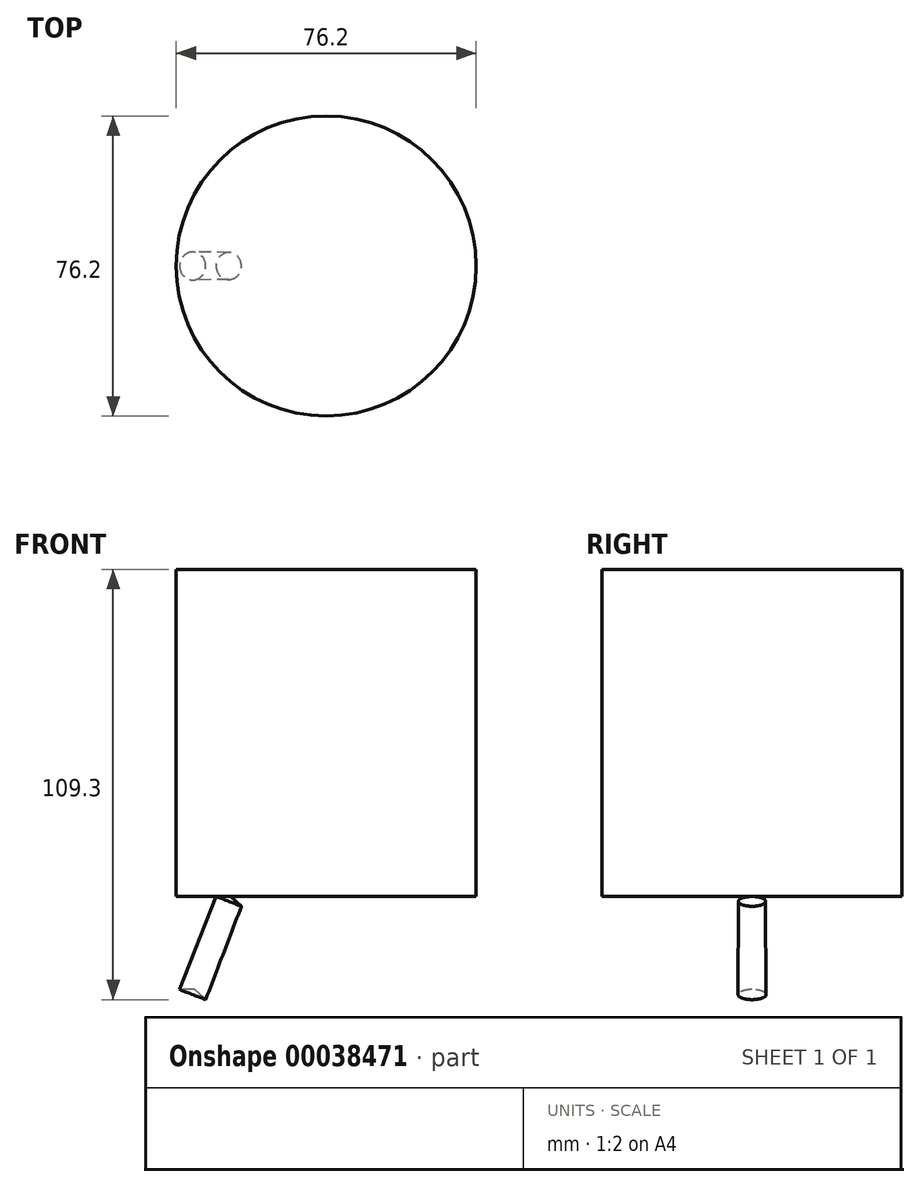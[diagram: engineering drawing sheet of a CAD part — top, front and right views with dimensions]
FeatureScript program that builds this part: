
annotation { "Feature Type Name" : "Feature", "Feature Type Description" : "" }
export const myFeature = defineFeature(function(context is Context, id is Id, definition is map)
    precondition{}
    {
        {
            var Q0;
            Q0=qCreatedBy(makeId("Front.planeOp"),FACE);
            var sketch = newSketch(context, id + "F0", { "sketchPlane" : qUnion([Q0])});
            skLineSegment(sketch, "E0.bottom", {"start": v(-36.45, 35.88) * mm, "end": v(39.75, 35.88) * mm});
            skLineSegment(sketch, "E0.top", {"start": v(-36.45, -21.09) * mm, "end": v(39.75, -21.09) * mm});
            skLineSegment(sketch, "E0.left", {"start": v(-36.45, 35.88) * mm, "end": v(-36.45, -21.09) * mm});
            skLineSegment(sketch, "E0.right", {"start": v(39.75, 35.88) * mm, "end": v(39.75, -21.09) * mm});
            skLineSegment(sketch, "E1.top", {"start": v(-36.45, -47.2) * mm, "end": v(39.75, -47.2) * mm});
            skLineSegment(sketch, "E1.left", {"start": v(-36.45, -21.09) * mm, "end": v(-36.45, -47.2) * mm});
            skLineSegment(sketch, "E1.right", {"start": v(39.75, -21.09) * mm, "end": v(39.75, -47.2) * mm});
            skLineSegment(sketch, "E2", {"start": v(-26.3, -47.2) * mm, "end": v(-35.57, -70.85) * mm});
            skLineSegment(sketch, "E3", {"start": v(-35.57, -70.85) * mm, "end": v(-27.95, -70.85) * mm});
            skLineSegment(sketch, "E4", {"start": v(-27.95, -70.85) * mm, "end": v(-18.67, -47.2) * mm});
            skLineSegment(sketch, "E5", {"start": v(1.65, 35.88) * mm, "end": v(1.65, -47.2) * mm});
            skLineSegment(sketch, "E6", {"start": v(1.65, -47.2) * mm, "end": v(1.65, -78.48) * mm});
            skLineSegment(sketch, "E7", {"start": v(-22.6, -47.2) * mm, "end": v(-31.76, -70.85) * mm});
            skSolve(sketch);
        }
        {
            var Q0;
            {var subQ0=sQuery(id+"F0.wireOp",EDGE,"E2");Q0=makeQuery(id+"F0.imprint","IMPRINT",FACE,{"disambiguationData":[TD([[makeQuery(id+"F0.imprint","IMPRINT",EDGE,{"derivedFrom":subQ0}),1.0]])]});}
            var Q1;
            Q1=sQuery(id+"F0.wireOp",EDGE,"E7");
            revolve(context, id + "F1", {"entities" : qUnion([Q0]), "axis" : qUnion([Q1]), "revolveType" : RevolveType.FULL});
        }
        {
            var Q0;
            {var subQ0=sQuery(id+"F0.wireOp",EDGE,"E0.left");Q0=makeQuery(id+"F0.imprint","IMPRINT",FACE,{"disambiguationData":[TD([[makeQuery(id+"F0.imprint","IMPRINT",EDGE,{"derivedFrom":subQ0}),1.0]])]});}
            var Q1;
            {var subQ8=sQuery(id+"F0.wireOp",EDGE,"E1.left");Q1=makeQuery(id+"F0.imprint","IMPRINT",FACE,{"disambiguationData":[TD([[makeQuery(id+"F0.imprint","IMPRINT",EDGE,{"derivedFrom":subQ8}),1.0]])]});}
            var Q2;
            Q2=sQuery(id+"F0.wireOp",EDGE,"E5");
            revolve(context, id + "F2", {"operationType" : NewBodyOperationType.ADD, "entities" : qUnion([Q0, Q1]), "axis" : qUnion([Q2]), "revolveType" : RevolveType.FULL});
        }
    });
